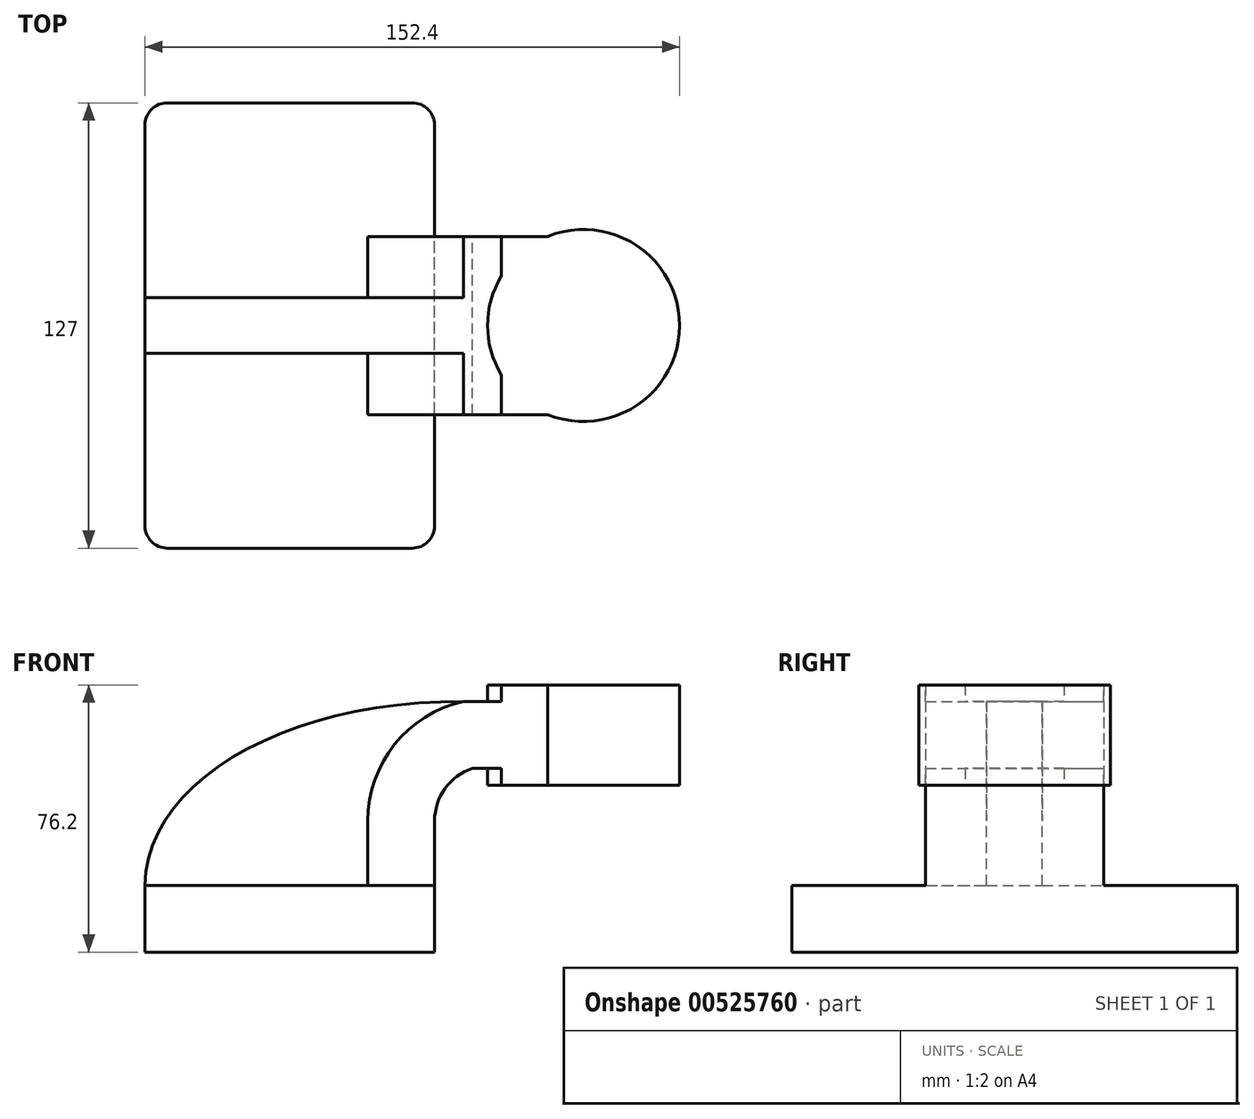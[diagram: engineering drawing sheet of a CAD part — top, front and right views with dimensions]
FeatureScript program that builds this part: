
annotation { "Feature Type Name" : "Feature", "Feature Type Description" : "" }
export const myFeature = defineFeature(function(context is Context, id is Id, definition is map)
    precondition{}
    {
        {
            var Q0;
            Q0=qCreatedBy(makeId("Front.planeOp"),FACE);
            var sketch = newSketch(context, id + "F0", { "sketchPlane" : qUnion([Q0])});
            skLineSegment(sketch, "E0.bottom", {"start": v(41.28, -9.52) * mm, "end": v(-41.27, -9.53) * mm});
            skLineSegment(sketch, "E0.top", {"start": v(41.27, 9.53) * mm, "end": v(-41.28, 9.53) * mm});
            skLineSegment(sketch, "E0.left", {"start": v(41.28, -9.52) * mm, "end": v(41.27, 9.53) * mm});
            skLineSegment(sketch, "E0.right", {"start": v(-41.27, -9.52) * mm, "end": v(-41.28, 9.53) * mm});
            skPoint(sketch, "E0.middle", {"position": v(0, 0) * mm});
            skLineSegment(sketch, "E1.bottom", {"start": v(111.12, 38.1) * mm, "end": v(60.32, 38.1) * mm});
            skLineSegment(sketch, "E1.top", {"start": v(111.12, 66.68) * mm, "end": v(60.32, 66.68) * mm});
            skLineSegment(sketch, "E1.left", {"start": v(111.12, 38.1) * mm, "end": v(111.12, 66.68) * mm});
            skLineSegment(sketch, "E1.right", {"start": v(60.32, 38.1) * mm, "end": v(60.32, 66.68) * mm});
            skPoint(sketch, "E1.middle", {"position": v(85.72, 52.39) * mm});
            skLineSegment(sketch, "E2", {"start": v(41.27, 9.53) * mm, "end": v(41.27, 27.85) * mm});
            skArc(sketch, "E3", {"start": v(52.01, 42.88) * mm, "mid": v(44.24, 37.09) * mm, "end": v(41.28, 27.85) * mm});
            skLineSegment(sketch, "E4", {"start": v(52.01, 42.88) * mm, "end": v(83.76, 42.88) * mm});
            skLineSegment(sketch, "E5.0", {"start": v(49.47, 61.93) * mm, "end": v(83.76, 61.93) * mm});
            skArc(sketch, "E5.1", {"start": v(49.47, 61.93) * mm, "mid": v(29.87, 49.67) * mm, "end": v(22.23, 27.85) * mm});
            skLineSegment(sketch, "E5.2", {"start": v(22.22, 9.53) * mm, "end": v(22.22, 27.85) * mm});
            skLineSegment(sketch, "E6", {"start": v(83.76, 42.88) * mm, "end": v(83.76, 61.93) * mm});
            skLineSegment(sketch, "E7", {"start": v(83.76, 42.88) * mm, "end": v(83.76, 38.1) * mm});
            skPoint(sketch, "E7.endSnap0", {"position": v(85.72, 38.1) * mm});
            skLineSegment(sketch, "E8", {"start": v(83.76, 61.93) * mm, "end": v(83.76, 66.68) * mm});
            skFitSpline(sketch, "E9", {"points": [v(-41.28, 9.53) * mm, v(49.47, 61.93) * mm], "startDerivative": vector(1.78, 91.07) * mm, "endDerivative": vector(148.42, -0.94) * mm});
            skSolve(sketch);
        }
        {
            var Q0;
            Q0=makeQuery(id+"F0.imprint","IMPRINT",FACE,{"disambiguationData":[TD([[makeQuery(id+"F0.imprint","IMPRINT",EDGE,{"derivedFrom":sQuery(id+"F0.wireOp",EDGE,"E0.bottom")}),-1.0]])]});
            extrude(context, id + "F1", {"entities" : qUnion([Q0]), "endBound" : BoundingType.SYMMETRIC, "depth" : 127 * mm, "offsetDistance" : 25.4 * mm});
        }
        {
            var Q0;
            {var subQ1=sQuery(id+"F0.wireOp",EDGE,"E2");Q0=makeQuery(id+"F0.imprint","IMPRINT",FACE,{"disambiguationData":[TD([[makeQuery(id+"F0.imprint","IMPRINT",EDGE,{"derivedFrom":subQ1}),1.0]])]});}
            var Q1;
            {var subQ5=sQuery(id+"F0.wireOp",EDGE,"E6");Q1=makeQuery(id+"F0.imprint","IMPRINT",FACE,{"disambiguationData":[TD([[makeQuery(id+"F0.imprint","IMPRINT",EDGE,{"derivedFrom":subQ5}),1.0]])]});}
            var Q2;
            {var subQ3=sQuery(id+"F0.wireOp",EDGE,"E8");Q2=makeQuery(id+"F0.imprint","IMPRINT",FACE,{"disambiguationData":[TD([[makeQuery(id+"F0.imprint","IMPRINT",EDGE,{"derivedFrom":subQ3}),1.0]])]});}
            var Q3;
            {var subQ3=sQuery(id+"F0.wireOp",EDGE,"E7");Q3=makeQuery(id+"F0.imprint","IMPRINT",FACE,{"disambiguationData":[TD([[makeQuery(id+"F0.imprint","IMPRINT",EDGE,{"derivedFrom":subQ3}),-1.0]])]});}
            extrude(context, id + "F2", {"entities" : qUnion([Q0, Q1, Q2, Q3]), "operationType" : NewBodyOperationType.ADD, "endBound" : BoundingType.SYMMETRIC, "depth" : 50.8 * mm, "offsetDistance" : 25.4 * mm});
        }
        {
            var Q0;
            Q0=makeQuery(id+"F0.imprint","IMPRINT",FACE,{"disambiguationData":[TD([[makeQuery(id+"F0.imprint","IMPRINT",EDGE,{"derivedFrom":sQuery(id+"F0.wireOp",EDGE,"E5.1")}),-1.0]])]});
            extrude(context, id + "F3", {"entities" : qUnion([Q0]), "operationType" : NewBodyOperationType.ADD, "endBound" : BoundingType.SYMMETRIC, "depth" : 15.88 * mm, "offsetDistance" : 25.4 * mm});
        }
        {
            var Q0;
            {var subQ0=sQuery(id+"F0.wireOp",EDGE,"E1.left");Q0=makeQuery(id+"F0.imprint","IMPRINT",FACE,{"disambiguationData":[TD([[makeQuery(id+"F0.imprint","IMPRINT",EDGE,{"derivedFrom":subQ0}),1.0]])]});}
            var Q1;
            Q1=sQuery(id+"F0.wireOp",EDGE,"E6");
            revolve(context, id + "F4", {"operationType" : NewBodyOperationType.ADD, "entities" : qUnion([Q0]), "axis" : qUnion([Q1]), "revolveType" : RevolveType.FULL});
        }
        {
            var Q0;
            Q0=makeQuery(id+"F1.opExtrude","CAP_EDGE",EDGE,{"disambiguationData":[OSD([sQuery(id+"F0.wireOp",EDGE,"E0.left")])],"isStart":false});
            var Q1;
            Q1=makeQuery(id+"F1.opExtrude","CAP_EDGE",EDGE,{"disambiguationData":[OSD([sQuery(id+"F0.wireOp",EDGE,"E0.left")])],"isStart":true});
            var Q2;
            Q2=makeQuery(id+"F1.opExtrude","CAP_EDGE",EDGE,{"disambiguationData":[OSD([sQuery(id+"F0.wireOp",EDGE,"E0.right")])],"isStart":true});
            var Q3;
            Q3=makeQuery(id+"F1.opExtrude","CAP_EDGE",EDGE,{"disambiguationData":[OSD([sQuery(id+"F0.wireOp",EDGE,"E0.right")])],"isStart":false});
            fillet(context, id + "F5", {"entities" : qUnion([Q0, Q1, Q2, Q3]), "radius" : 6.35 * mm, "tangentPropagation" : true, "allowEdgeOverflow" : false});
        }
    });
